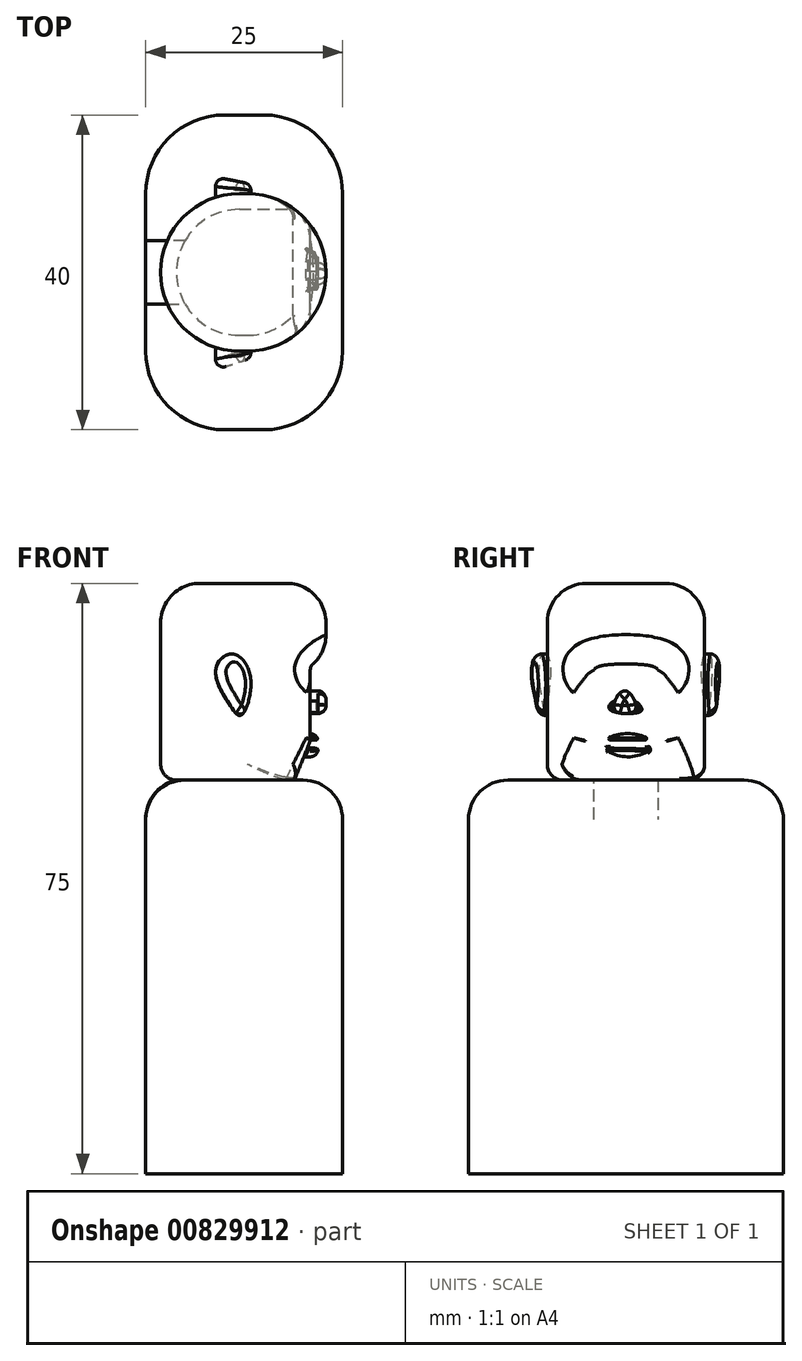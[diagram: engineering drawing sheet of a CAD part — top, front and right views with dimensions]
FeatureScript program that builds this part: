
annotation { "Feature Type Name" : "Feature", "Feature Type Description" : "" }
export const myFeature = defineFeature(function(context is Context, id is Id, definition is map)
    precondition{}
    {
        {
            var Q0;
            Q0=qCreatedBy(makeId("Front.planeOp"),FACE);
            var sketch = newSketch(context, id + "F0", { "sketchPlane" : qUnion([Q0])});
            skLineSegment(sketch, "E0.bottom", {"start": v(-6.1, 25) * mm, "end": v(14.9, 25) * mm});
            skLineSegment(sketch, "E0.top", {"start": v(12.9, 15) * mm, "end": v(14.9, 15) * mm});
            skLineSegment(sketch, "E0.left", {"start": v(-6.1, 25) * mm, "end": v(-6.1, 15) * mm});
            skLineSegment(sketch, "E0.right", {"start": v(14.9, 25) * mm, "end": v(14.9, 15) * mm});
            skLineSegment(sketch, "E1.top", {"start": v(-5.1, 0) * mm, "end": v(10.9, 0) * mm});
            skLineSegment(sketch, "E1.left", {"start": v(-6.1, 15) * mm, "end": v(-6.1, 1) * mm});
            skLineSegment(sketch, "E1.right", {"start": v(12.9, 15) * mm, "end": v(12.9, 5) * mm});
            skLineSegment(sketch, "E2", {"start": v(12.9, 5) * mm, "end": v(10.9, 0) * mm});
            skPoint(sketch, "E3.orphan", {"position": v(12.9, 0) * mm});
            skLineSegment(sketch, "E4", {"start": v(-6.1, 1) * mm, "end": v(-5.1, 0) * mm});
            skPoint(sketch, "E5.orphan", {"position": v(-6.1, 0) * mm});
            skSolve(sketch);
        }
        {
            var Q0;
            Q0 = qSketchRegion(id + "F0", true);
            extrude(context, id + "F1", {"entities" : qUnion([Q0]), "depth" : 20 * mm, "offsetDistance" : 25 * mm});
        }
        {
            var Q0;
            Q0=makeQuery(id+"F1.opExtrude","CAP_EDGE",EDGE,{"disambiguationData":[OSD([sQuery(id+"F0.wireOp",EDGE,"E0.right")])],"isStart":false});
            var Q1;
            Q1=makeQuery(id+"F1.opExtrude","CAP_EDGE",EDGE,{"disambiguationData":[OSD([sQuery(id+"F0.wireOp",EDGE,"E0.right")])],"isStart":true});
            var Q2;
            Q2=makeQuery(id+"F1.opExtrude","CAP_EDGE",EDGE,{"disambiguationData":[OSD([sQuery(id+"F0.wireOp",EDGE,"E0.left"),sQuery(id+"F0.wireOp",EDGE,"E1.left")])],"isStart":true});
            var Q3;
            Q3=makeQuery(id+"F1.opExtrude","CAP_EDGE",EDGE,{"disambiguationData":[OSD([sQuery(id+"F0.wireOp",EDGE,"E0.left"),sQuery(id+"F0.wireOp",EDGE,"E1.left")])],"isStart":false});
            fillet(context, id + "F2", {"entities" : qUnion([Q0, Q1, Q2, Q3]), "radius" : 10 * mm, "tangentPropagation" : true, "allowEdgeOverflow" : false});
        }
        {
            var Q0;
            Q0=makeQuery(id+"F2.opFillet","BLEND_EDGE",EDGE,{"blendedFrom":[makeQuery(id+"F1.opExtrude","CAP_EDGE",EDGE,{"disambiguationData":[OSD([sQuery(id+"F0.wireOp",EDGE,"E0.right")])],"isStart":true}),makeQuery(id+"F1.opExtrude","SWEPT_FACE",FACE,{"disambiguationData":[OSD([sQuery(id+"F0.wireOp",EDGE,"E0.bottom")])]})],"blendedInto":[makeQuery(id+"F1.opExtrude","SWEPT_FACE",FACE,{"disambiguationData":[OSD([sQuery(id+"F0.wireOp",EDGE,"E0.bottom")])]})]});
            fillet(context, id + "F3", {"entities" : qUnion([Q0]), "radius" : 5 * mm, "tangentPropagation" : true, "allowEdgeOverflow" : false});
        }
        {
            var Q0;
            Q0=makeQuery(id+"F2.opFillet","BLEND_EDGE",EDGE,{"blendedFrom":[makeQuery(id+"F1.opExtrude","CAP_EDGE",EDGE,{"disambiguationData":[OSD([sQuery(id+"F0.wireOp",EDGE,"E0.right")])],"isStart":false}),makeQuery(id+"F1.opExtrude","SWEPT_FACE",FACE,{"disambiguationData":[OSD([sQuery(id+"F0.wireOp",EDGE,"E1.top")])]})],"blendedInto":[makeQuery(id+"F1.opExtrude","SWEPT_FACE",FACE,{"disambiguationData":[OSD([sQuery(id+"F0.wireOp",EDGE,"E1.top")])]})]});
            var Q1;
            Q1=makeQuery(id+"F2.opFillet","BLEND_EDGE",EDGE,{"blendedFrom":[makeQuery(id+"F1.opExtrude","CAP_EDGE",EDGE,{"disambiguationData":[OSD([sQuery(id+"F0.wireOp",EDGE,"E0.right")])],"isStart":false}),makeQuery(id+"F1.opExtrude","SWEPT_FACE",FACE,{"disambiguationData":[OSD([sQuery(id+"F0.wireOp",EDGE,"E1.right")])]})],"blendedInto":[makeQuery(id+"F1.opExtrude","SWEPT_FACE",FACE,{"disambiguationData":[OSD([sQuery(id+"F0.wireOp",EDGE,"E1.right")])]})]});
            var Q2;
            Q2=makeQuery(id+"F2.opFillet","BLEND_EDGE",EDGE,{"blendedFrom":[makeQuery(id+"F1.opExtrude","CAP_EDGE",EDGE,{"disambiguationData":[OSD([sQuery(id+"F0.wireOp",EDGE,"E0.right")])],"isStart":false}),makeQuery(id+"F1.opExtrude","SWEPT_FACE",FACE,{"disambiguationData":[OSD([sQuery(id+"F0.wireOp",EDGE,"E2")])]})],"blendedInto":[makeQuery(id+"F1.opExtrude","SWEPT_FACE",FACE,{"disambiguationData":[OSD([sQuery(id+"F0.wireOp",EDGE,"E2")])]})]});
            var Q3;
            Q3=makeQuery(id+"F2.opFillet","BLEND_EDGE",EDGE,{"blendedFrom":[makeQuery(id+"F1.opExtrude","CAP_EDGE",EDGE,{"disambiguationData":[OSD([sQuery(id+"F0.wireOp",EDGE,"E0.right")])],"isStart":true}),makeQuery(id+"F1.opExtrude","SWEPT_FACE",FACE,{"disambiguationData":[OSD([sQuery(id+"F0.wireOp",EDGE,"E1.right")])]})],"blendedInto":[makeQuery(id+"F1.opExtrude","SWEPT_FACE",FACE,{"disambiguationData":[OSD([sQuery(id+"F0.wireOp",EDGE,"E1.right")])]})]});
            var Q4;
            Q4=makeQuery(id+"F2.opFillet","BLEND_EDGE",EDGE,{"blendedFrom":[makeQuery(id+"F1.opExtrude","CAP_EDGE",EDGE,{"disambiguationData":[OSD([sQuery(id+"F0.wireOp",EDGE,"E0.right")])],"isStart":true}),makeQuery(id+"F1.opExtrude","SWEPT_FACE",FACE,{"disambiguationData":[OSD([sQuery(id+"F0.wireOp",EDGE,"E2")])]})],"blendedInto":[makeQuery(id+"F1.opExtrude","SWEPT_FACE",FACE,{"disambiguationData":[OSD([sQuery(id+"F0.wireOp",EDGE,"E2")])]})]});
            fillet(context, id + "F4", {"entities" : qUnion([Q0, Q1, Q2, Q3, Q4]), "radius" : 2 * mm, "tangentPropagation" : true, "allowEdgeOverflow" : false});
        }
        {
            var Q0;
            Q0=makeQuery(id+"F1.opExtrude","SWEPT_EDGE",EDGE,{"disambiguationData":[OSD([sQuery(id+"F0.wireOp",EDGE,"E0.top"),sQuery(id+"F0.wireOp",EDGE,"E1.right")])]});
            fillet(context, id + "F5", {"entities" : qUnion([Q0]), "radius" : 1 * mm, "tangentPropagation" : true, "allowEdgeOverflow" : false});
        }
        {
            var Q0;
            Q0=makeQuery(id+"F2.opFillet","BLEND_EDGE",EDGE,{"blendedFrom":[makeQuery(id+"F1.opExtrude","CAP_EDGE",EDGE,{"disambiguationData":[OSD([sQuery(id+"F0.wireOp",EDGE,"E0.right")])],"isStart":true}),makeQuery(id+"F1.opExtrude","SWEPT_FACE",FACE,{"disambiguationData":[OSD([sQuery(id+"F0.wireOp",EDGE,"E0.top")])]})],"blendedInto":[makeQuery(id+"F1.opExtrude","SWEPT_FACE",FACE,{"disambiguationData":[OSD([sQuery(id+"F0.wireOp",EDGE,"E0.top")])]})]});
            fillet(context, id + "F6", {"entities" : qUnion([Q0]), "radius" : 5 * mm, "tangentPropagation" : true, "allowEdgeOverflow" : false});
        }
        {
            var Q0;
            Q0=makeQuery(id+"F1.opExtrude","SWEPT_FACE",FACE,{"disambiguationData":[OSD([sQuery(id+"F0.wireOp",EDGE,"E1.right")])]});
            var sketch = newSketch(context, id + "F7", { "sketchPlane" : qUnion([Q0])});
            skArc(sketch, "E6", {"start": v(-6.73, 5.07) * mm, "mid": v(-9.78, 5.91) * mm, "end": v(-12.84, 5.07) * mm});
            skArc(sketch, "E7", {"start": v(-12.84, 4.07) * mm, "mid": v(-9.8, 2.95) * mm, "end": v(-6.73, 3.94) * mm});
            skLineSegment(sketch, "E8", {"start": v(-12.84, 4.07) * mm, "end": v(-6.73, 3.94) * mm});
            skLineSegment(sketch, "E9", {"start": v(-12.84, 5.07) * mm, "end": v(-6.73, 5.07) * mm});
            skSolve(sketch);
        }
        {
            var Q0;
            Q0 = qSketchRegion(id + "F7", true);
            extrude(context, id + "F8", {"entities" : qUnion([Q0]), "operationType" : NewBodyOperationType.ADD, "endBound" : BoundingType.SYMMETRIC, "depth" : 2 * mm, "offsetDistance" : 25 * mm});
        }
        {
            var Q0;
            Q0=makeQuery(id+"F8.opExtrude","CAP_EDGE",EDGE,{"disambiguationData":[OSD([sQuery(id+"F7.wireOp",EDGE,"E6")])],"isStart":false});
            fillet(context, id + "F9", {"entities" : qUnion([Q0]), "radius" : 1 * mm, "tangentPropagation" : true, "allowEdgeOverflow" : false});
        }
        {
            var Q0;
            Q0=makeQuery(id+"F8.opExtrude","CAP_EDGE",EDGE,{"disambiguationData":[OSD([sQuery(id+"F7.wireOp",EDGE,"E7")])],"isStart":false});
            fillet(context, id + "F10", {"entities" : qUnion([Q0]), "radius" : 1 * mm, "tangentPropagation" : true, "allowEdgeOverflow" : false});
        }
        {
            var Q0;
            Q0=makeQuery(id+"F10.opFillet","BLEND_EDGE",EDGE,{"blendedFrom":[makeQuery(id+"F8.opExtrude","CAP_EDGE",EDGE,{"disambiguationData":[OSD([sQuery(id+"F7.wireOp",EDGE,"E7")])],"isStart":false}),makeQuery(id+"F8.opExtrude","SWEPT_FACE",FACE,{"disambiguationData":[OSD([sQuery(id+"F7.wireOp",EDGE,"E8")])]})],"blendedInto":[makeQuery(id+"F8.opExtrude","SWEPT_FACE",FACE,{"disambiguationData":[OSD([sQuery(id+"F7.wireOp",EDGE,"E8")])]})]});
            var Q1;
            Q1=makeQuery(id+"F9.opFillet","BLEND_EDGE",EDGE,{"blendedFrom":[makeQuery(id+"F8.opExtrude","CAP_EDGE",EDGE,{"disambiguationData":[OSD([sQuery(id+"F7.wireOp",EDGE,"E6")])],"isStart":false}),makeQuery(id+"F8.opExtrude","SWEPT_FACE",FACE,{"disambiguationData":[OSD([sQuery(id+"F7.wireOp",EDGE,"5WrQf7PE-4mQL-KW4R-NzSd-7Rb408GSEZBa")])]})],"blendedInto":[makeQuery(id+"F8.opExtrude","SWEPT_FACE",FACE,{"disambiguationData":[OSD([sQuery(id+"F7.wireOp",EDGE,"5WrQf7PE-4mQL-KW4R-NzSd-7Rb408GSEZBa")])]})]});
            fillet(context, id + "F11", {"entities" : qUnion([Q0, Q1]), "radius" : 0.2 * mm, "tangentPropagation" : true, "allowEdgeOverflow" : false});
        }
        {
            var Q0;
            Q0=makeQuery(id+"F1.opExtrude","SWEPT_FACE",FACE,{"disambiguationData":[OSD([sQuery(id+"F0.wireOp",EDGE,"E2")])]});
            fillet(context, id + "F12", {"entities" : qUnion([Q0]), "radius" : 0.3 * mm, "tangentPropagation" : true, "allowEdgeOverflow" : false});
        }
        {
            var Q0;
            Q0=makeQuery(id+"F9.opFillet","BLEND_EDGE",EDGE,{"blendedFrom":[makeQuery(id+"F8.opExtrude","CAP_EDGE",EDGE,{"disambiguationData":[OSD([sQuery(id+"F7.wireOp",EDGE,"E6")])],"isStart":false}),makeQuery(id+"F8.opExtrude","SWEPT_FACE",FACE,{"disambiguationData":[OSD([sQuery(id+"F7.wireOp",EDGE,"E9")])]})],"blendedInto":[makeQuery(id+"F8.opExtrude","SWEPT_FACE",FACE,{"disambiguationData":[OSD([sQuery(id+"F7.wireOp",EDGE,"E9")])]})]});
            fillet(context, id + "F13", {"entities" : qUnion([Q0]), "radius" : 0.2 * mm, "tangentPropagation" : true, "allowEdgeOverflow" : false});
        }
        {
            var Q0;
            Q0=qCreatedBy(makeId("Front.planeOp"),FACE);
            var sketch = newSketch(context, id + "F14", { "sketchPlane" : qUnion([Q0])});
            skFitSpline(sketch, "E10", {"points": [v(5.15, 13.8) * mm, v(2.93, 16.02) * mm, v(0.9, 14.11) * mm, v(2.55, 9.73) * mm, v(3.95, 8.21) * mm, v(4.83, 9.35) * mm, v(5.15, 13.8) * mm]});
            skSolve(sketch);
        }
        {
            var Q0;
            Q0 = qSketchRegion(id + "F14", true);
            extrude(context, id + "F15", {"entities" : qUnion([Q0]), "operationType" : NewBodyOperationType.ADD, "depth" : 23 * mm, "offsetDistance" : 25 * mm, "hasSecondDirection" : true, "secondDirectionOppositeDirection" : true, "secondDirectionDepth" : 3 * mm});
        }
        {
            var Q0;
            Q0=qCreatedBy(makeId("Top.planeOp"),FACE);
            var sketch = newSketch(context, id + "F16", { "sketchPlane" : qUnion([Q0])});
            skLineSegment(sketch, "E11", {"start": v(0, -22.7) * mm, "end": v(6.73, -20.45) * mm});
            skLineSegment(sketch, "E12", {"start": v(6.73, -20.45) * mm, "end": v(6.73, -24.2) * mm});
            skLineSegment(sketch, "E13", {"start": v(6.73, -24.2) * mm, "end": v(0, -24.2) * mm});
            skLineSegment(sketch, "E14", {"start": v(0, -24.2) * mm, "end": v(0, -22.7) * mm});
            skLineSegment(sketch, "E15", {"start": v(7.05, 0.9) * mm, "end": v(0, 2.28) * mm});
            skLineSegment(sketch, "E16", {"start": v(0, 2.28) * mm, "end": v(0, 4.63) * mm});
            skLineSegment(sketch, "E17", {"start": v(0, 4.63) * mm, "end": v(7.59, 4.63) * mm});
            skLineSegment(sketch, "E18", {"start": v(7.59, 4.63) * mm, "end": v(7.05, 0.9) * mm});
            skSolve(sketch);
        }
        {
            var Q0;
            Q0 = qSketchRegion(id + "F16", true);
            extrude(context, id + "F17", {"entities" : qUnion([Q0]), "operationType" : NewBodyOperationType.REMOVE, "depth" : 25 * mm, "offsetDistance" : 25 * mm});
        }
        {
            var Q0;
            {var subQ3=sQuery(id+"F14.wireOp",EDGE,"E10");Q0=makeQuery(id+"F17.boolean.opBoolean","INTERSECT",EDGE,{"derivedFrom":[makeQuery(id+"F15.boolean.opBoolean","SPLIT",FACE,{"disambiguationData":[TD([makeQuery(id+"F15.opExtrude","CAP_FACE",FACE,{"disambiguationData":[OSD([subQ3])],"isStart":false})])],"derivedFrom":makeQuery(id+"F15.opExtrude","SWEPT_FACE",FACE,{"disambiguationData":[OSD([subQ3])]})}),makeQuery(id+"F17.opExtrude","SWEPT_FACE",FACE,{"disambiguationData":[OSD([sQuery(id+"F16.wireOp",EDGE,"E11")])]})]});}
            var Q1;
            {var subQ3=sQuery(id+"F14.wireOp",EDGE,"E10");Q1=makeQuery(id+"F17.boolean.opBoolean","INTERSECT",EDGE,{"derivedFrom":[makeQuery(id+"F15.boolean.opBoolean","SPLIT",FACE,{"disambiguationData":[TD([makeQuery(id+"F15.opExtrude","CAP_FACE",FACE,{"disambiguationData":[OSD([subQ3])],"isStart":true})])],"derivedFrom":makeQuery(id+"F15.opExtrude","SWEPT_FACE",FACE,{"disambiguationData":[OSD([subQ3])]})}),makeQuery(id+"F17.opExtrude","SWEPT_FACE",FACE,{"disambiguationData":[OSD([sQuery(id+"F16.wireOp",EDGE,"E15")])]})]});}
            fillet(context, id + "F18", {"entities" : qUnion([Q0, Q1]), "radius" : 1 * mm, "tangentPropagation" : true, "allowEdgeOverflow" : false});
        }
        {
            var Q0;
            Q0=makeQuery(id+"F1.opExtrude","SWEPT_FACE",FACE,{"disambiguationData":[OSD([sQuery(id+"F0.wireOp",EDGE,"E1.right")])]});
            var sketch = newSketch(context, id + "F19", { "sketchPlane" : qUnion([Q0])});
            skFitSpline(sketch, "E19", {"points": [v(-10.2, 11.34) * mm, v(-8.75, 9.16) * mm, v(-10.06, 8.45) * mm, v(-11.49, 9.12) * mm, v(-10.2, 11.34) * mm]});
            skSolve(sketch);
        }
        {
            var Q0;
            Q0 = qSketchRegion(id + "F19", true);
            extrude(context, id + "F20", {"entities" : qUnion([Q0]), "operationType" : NewBodyOperationType.ADD, "depth" : 2 * mm, "offsetDistance" : 25 * mm});
        }
        {
            var Q0;
            Q0=makeQuery(id+"F20.opExtrude","CAP_EDGE",EDGE,{"disambiguationData":[OSD([sQuery(id+"F19.wireOp",EDGE,"E19")])],"isStart":false});
            fillet(context, id + "F21", {"entities" : qUnion([Q0]), "radius" : 1 * mm, "tangentPropagation" : true, "allowEdgeOverflow" : false});
        }
        {
            var Q0;
            Q0=makeQuery(id+"F1.opExtrude","SWEPT_FACE",FACE,{"disambiguationData":[OSD([sQuery(id+"F0.wireOp",EDGE,"E1.right")])]});
            var sketch = newSketch(context, id + "F22", { "sketchPlane" : qUnion([Q0])});
            skFitSpline(sketch, "E20", {"points": [v(-11.38, 10.06) * mm, v(-12.17, 9.16) * mm, v(-10.97, 8.57) * mm, v(-8.85, 8.51) * mm, v(-7.99, 8.9) * mm, v(-8.34, 9.63) * mm, v(-8.88, 10) * mm, v(-11.38, 10.06) * mm]});
            skSolve(sketch);
        }
        {
            var Q0;
            Q0 = qSketchRegion(id + "F22", true);
            extrude(context, id + "F23", {"entities" : qUnion([Q0]), "operationType" : NewBodyOperationType.ADD, "depth" : 1 * mm, "offsetDistance" : 25 * mm});
        }
        {
            var Q0;
            {var subQ0=sQuery(id+"F19.wireOp",EDGE,"E19");var subQ1=sQuery(id+"F22.wireOp",EDGE,"E20");Q0=makeQuery(id+"F23.boolean.opBoolean","SPLIT",EDGE,{"disambiguationData":[TD([makeQuery(id+"F21.opFillet","BLEND_FACE",FACE,{"disambiguationData":[OSD([subQ0]),OD(0.0)]})])],"derivedFrom":makeQuery(id+"F23.opExtrude","CAP_EDGE",EDGE,{"disambiguationData":[OSD([subQ1])],"isStart":false})});}
            var Q1;
            {var subQ0=sQuery(id+"F19.wireOp",EDGE,"E19");var subQ1=sQuery(id+"F22.wireOp",EDGE,"E20");Q1=makeQuery(id+"F23.boolean.opBoolean","SPLIT",EDGE,{"disambiguationData":[TD([makeQuery(id+"F21.opFillet","BLEND_FACE",FACE,{"disambiguationData":[OSD([subQ0]),OD(4.0)]})])],"derivedFrom":makeQuery(id+"F23.opExtrude","CAP_EDGE",EDGE,{"disambiguationData":[OSD([subQ1])],"isStart":false})});}
            fillet(context, id + "F24", {"entities" : qUnion([Q0, Q1]), "radius" : 0.25 * mm, "tangentPropagation" : true, "allowEdgeOverflow" : false});
        }
        {
            var Q0;
            Q0=makeQuery(id+"F1.opExtrude","SWEPT_FACE",FACE,{"disambiguationData":[OSD([sQuery(id+"F0.wireOp",EDGE,"E1.top")])]});
            var sketch = newSketch(context, id + "F25", { "sketchPlane" : qUnion([Q0])});
            skLineSegment(sketch, "E21.bottom", {"start": v(17, -10) * mm, "end": v(-8, -10) * mm});
            skLineSegment(sketch, "E21.top", {"start": v(17, 30) * mm, "end": v(-8, 30) * mm});
            skLineSegment(sketch, "E21.left", {"start": v(17, -10) * mm, "end": v(17, 30) * mm});
            skLineSegment(sketch, "E21.right", {"start": v(-8, -10) * mm, "end": v(-8, 30) * mm});
            skSolve(sketch);
        }
        {
            var Q0;
            {var subQ0=sQuery(id+"F0.wireOp",EDGE,"E1.top");var subQ1=makeQuery(id+"F1.opExtrude","SWEPT_FACE",FACE,{"disambiguationData":[OSD([subQ0])]});var subQ2=subQ1;Q0=makeQuery(id+"F25.imprint","IMPRINT",FACE,{"disambiguationData":[TD([[makeQuery(id+"F25.imprint","IMPRINT",EDGE,{"derivedFrom":makeQuery(id+"F4.opFillet","BLEND_EDGE",EDGE,{"blendedFrom":[makeQuery(id+"F1.opExtrude","CAP_EDGE",EDGE,{"disambiguationData":[OSD([subQ0])],"isStart":false}),subQ2],"blendedInto":[subQ2]})}),1.0]])]});}
            var sketch = newSketch(context, id + "F26", { "sketchPlane" : qUnion([Q0])});
            skCircle(sketch, "E22", {"center": v(2.37, 10) * mm, "radius": 1.77 * mm});
            skSolve(sketch);
        }
        {
            var Q0;
            Q0 = qSketchRegion(id + "F26", true);
            extrude(context, id + "F27", {"entities" : qUnion([Q0]), "operationType" : NewBodyOperationType.ADD, "endBound" : BoundingType.SYMMETRIC, "depth" : 25 * mm, "offsetDistance" : 25 * mm});
        }
        {
            var Q0;
            Q0 = qSketchRegion(id + "F25", true);
            extrude(context, id + "F28", {"entities" : qUnion([Q0]), "operationType" : NewBodyOperationType.ADD, "depth" : 50 * mm, "offsetDistance" : 25 * mm});
        }
        {
            var Q0;
            Q0=makeQuery(id+"F28.opExtrude","SWEPT_EDGE",EDGE,{"disambiguationData":[OSD([sQuery(id+"F25.wireOp",EDGE,"E21.bottom"),sQuery(id+"F25.wireOp",EDGE,"E21.left")])]});
            var Q1;
            Q1=makeQuery(id+"F28.opExtrude","SWEPT_EDGE",EDGE,{"disambiguationData":[OSD([sQuery(id+"F25.wireOp",EDGE,"E21.bottom"),sQuery(id+"F25.wireOp",EDGE,"E21.right")])]});
            var Q2;
            Q2=makeQuery(id+"F28.opExtrude","SWEPT_EDGE",EDGE,{"disambiguationData":[OSD([sQuery(id+"F25.wireOp",EDGE,"E21.top"),sQuery(id+"F25.wireOp",EDGE,"E21.right")])]});
            var Q3;
            Q3=makeQuery(id+"F28.opExtrude","SWEPT_EDGE",EDGE,{"disambiguationData":[OSD([sQuery(id+"F25.wireOp",EDGE,"E21.top"),sQuery(id+"F25.wireOp",EDGE,"E21.left")])]});
            fillet(context, id + "F29", {"entities" : qUnion([Q0, Q1, Q2, Q3]), "radius" : 10 * mm, "tangentPropagation" : true, "allowEdgeOverflow" : false});
        }
        {
            var Q0;
            Q0=makeQuery(id+"F28.opExtrude","CAP_EDGE",EDGE,{"disambiguationData":[OSD([sQuery(id+"F25.wireOp",EDGE,"E21.left")])],"isStart":true});
            fillet(context, id + "F30", {"entities" : qUnion([Q0]), "radius" : 5 * mm, "tangentPropagation" : true, "allowEdgeOverflow" : false});
        }
    });
